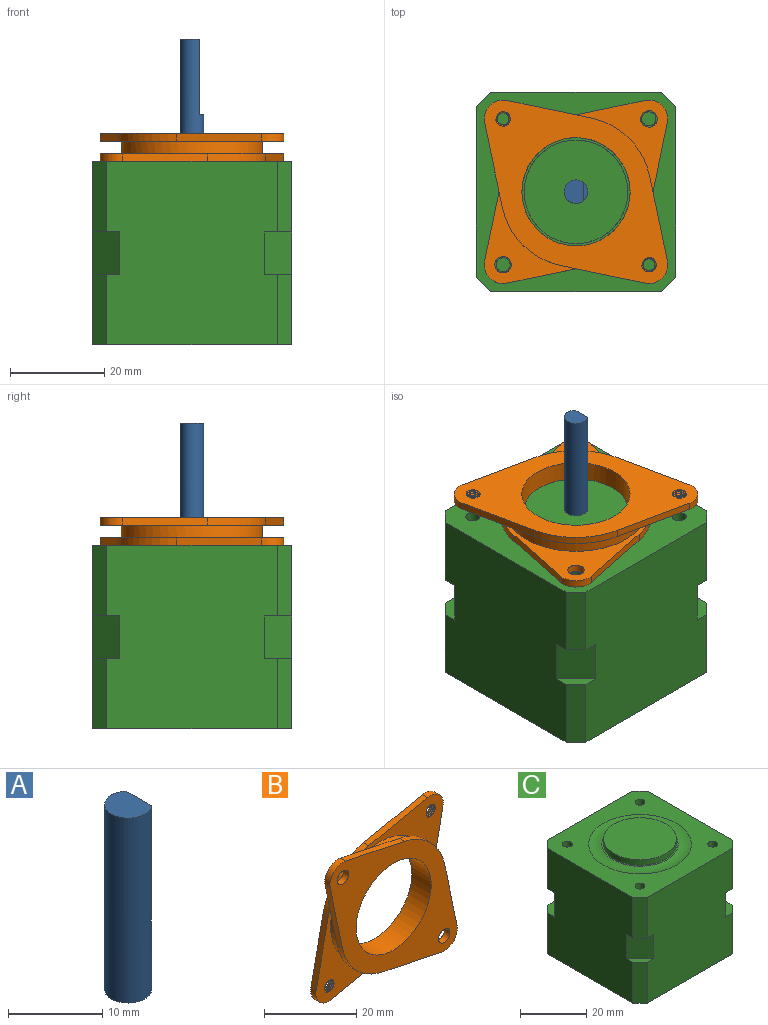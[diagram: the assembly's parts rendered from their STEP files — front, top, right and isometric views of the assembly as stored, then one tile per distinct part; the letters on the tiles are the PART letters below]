
ASSEMBLY  parts=3 mates=2
PART A: 5 faces, bbox 5x5x24 mm
  f0: cylinder r=2.5mm len=24mm, axis (0,0,-1), area 306.9mm2, adj f1,f2,f3,f4
  f1: plane 5x4.1mm, normal (0,0,1), area 17.2mm2, adj f0,f3
  f2: plane 5x5mm, normal (0,0,-1), area 19.6mm2, adj f0
  f3: plane 16x3.84mm, normal (1,0,0), area 61.5mm2, adj f0,f1,f4
  f4: plane 3.84x0.9mm, normal (0,0,1), area 2.4mm2, adj f0,f3
PART B: 32 faces, bbox 39.1x6.2x39.1 mm
  f0: cylinder r=1.75mm len=3.5mm, axis (0,1,0), area 17.6mm2, adj f10,f11
  f1: cylinder r=1.75mm len=3.5mm, axis (0,1,0), area 17.6mm2, adj f10,f11
  f2: plane 17.96x3.75mm, normal (-0.2,0,-0.98), area 29.3mm2, adj f3,f9,f10,f11
  f3: cylinder r=4mm len=4.82mm, axis (0,1,0), area 12.7mm2, adj f2,f4,f10,f11
  f4: plane 17.96x3.75mm, normal (0.98,0,0.2), area 29.3mm2, adj f3,f5,f10,f11
  f5: cylinder r=16mm len=12.39mm, axis (0,1,0), area 29.7mm2, adj f4,f6,f10,f11
  f6: plane 17.96x3.75mm, normal (0.2,0,0.98), area 29.3mm2, adj f5,f7,f10,f11
  f7: cylinder r=4mm len=4.82mm, axis (0,1,0), area 12.7mm2, adj f6,f8,f10,f11
  f8: plane 17.96x3.75mm, normal (-0.98,0,-0.2), area 29.3mm2, adj f7,f9,f10,f11
  f9: cylinder r=16mm len=12.39mm, axis (0,1,0), area 29.7mm2, adj f2,f8,f10,f11
  f10: plane 39x39mm, normal (0,1,0), area 336mm2, adj f0,f1,f2,f3,f4,f5,f6,f7
  f11: plane 39x39mm, normal (0,-1,0), area 627.4mm2, adj f0,f1,f2,f3,f4,f5,f6,f7
  f12: plane 39.14x39.14mm, normal (0,1,0), area 633.9mm2, adj f14,f15,f16,f17,f18,f19,f20,f21
  f13: cylinder r=15mm len=30mm, axis (0,1,0), area 254.5mm2, adj f10,f31
  f14: cylinder r=11.5mm len=23mm, axis (0,-1,0), area 426.3mm2, adj f11,f12
  f15: cylinder r=1.54mm len=3.09mm, axis (0,1,0), area 3.6mm2, adj f12,f16,f17,f31
  f16: bspline ~3.58x3.57mm, area 9.1mm2, adj f12,f15,f22,f31
  f17: bspline ~3.59x3.58mm, area 9.1mm2, adj f12,f15,f22,f31
  f18: cylinder r=1.54mm len=3.09mm, axis (0,1,0), area 3.6mm2, adj f12,f19,f20,f31
  f19: bspline ~3.58x3.57mm, area 9.1mm2, adj f12,f18,f21,f31
  f20: bspline ~3.59x3.58mm, area 9.1mm2, adj f12,f18,f21,f31
  f21: cylinder r=1.26mm len=2.53mm, axis (0,1,0), area 1.5mm2, adj f12,f19,f20,f31
  f22: cylinder r=1.26mm len=2.53mm, axis (0,1,0), area 1.5mm2, adj f12,f16,f17,f31
  f23: plane 17.96x3.75mm, normal (0.2,0,-0.98), area 29.3mm2, adj f12,f24,f30,f31
  f24: cylinder r=16mm len=12.39mm, axis (0,1,0), area 29.7mm2, adj f12,f23,f25,f31
  f25: plane 17.96x3.75mm, normal (0.98,0,-0.2), area 29.3mm2, adj f12,f24,f26,f31
  f26: cylinder r=4mm len=4.82mm, axis (0,1,0), area 12.7mm2, adj f12,f25,f27,f31
  f27: plane 17.96x3.75mm, normal (-0.2,0,0.98), area 29.3mm2, adj f12,f26,f28,f31
  f28: cylinder r=16mm len=12.39mm, axis (0,1,0), area 29.7mm2, adj f12,f27,f29,f31
  f29: plane 17.96x3.75mm, normal (-0.98,0,0.2), area 29.3mm2, adj f12,f28,f30,f31
  f30: cylinder r=4mm len=4.82mm, axis (0,1,0), area 12.7mm2, adj f12,f23,f29,f31
  f31: plane 39.14x39.14mm, normal (0,-1,0), area 342.6mm2, adj f13,f15,f16,f17,f18,f19,f20,f21
PART C: 58 faces, bbox 42.3x42.3x41.1 mm
  f0: cylinder r=2.5mm len=5mm, axis (0,0,1), area 15.7mm2, adj f1,f16
  f1: plane 5x5mm, normal (0,0,-1), area 19.6mm2, adj f0
  f2: plane 5.83x5.83mm, normal (0,0,1), area 12.5mm2, adj f5,f6,f7,f33
  f3: plane 5.83x5.83mm, normal (0,0,1), area 12.5mm2, adj f5,f11,f12,f34
  f4: plane 5.83x5.83mm, normal (0,0,1), area 12.5mm2, adj f9,f10,f11,f35
  f5: plane 39x36.3mm, normal (0,1,0), area 1364.8mm2, adj f2,f3,f6,f12,f14,f33,f34,f37
  f6: plane 15x3mm, normal (-0.71,0.71,0), area 63.6mm2, adj f2,f5,f7,f14
  f7: plane 39x36.3mm, normal (-1,0,0), area 1364.8mm2, adj f2,f6,f8,f13,f14,f33,f36,f37
  f8: plane 15x3mm, normal (-0.71,-0.71,0), area 63.6mm2, adj f7,f9,f13,f14
  f9: plane 39x36.3mm, normal (0,-1,0), area 1364.8mm2, adj f4,f8,f10,f13,f14,f35,f36,f37
  f10: plane 15x3mm, normal (0.71,-0.71,0), area 63.6mm2, adj f4,f9,f11,f14
  f11: plane 39x36.3mm, normal (1,0,0), area 1364.8mm2, adj f3,f4,f10,f12,f14,f34,f35,f37
  f12: plane 15x3mm, normal (0.71,0.71,0), area 63.6mm2, adj f3,f5,f11,f14
  f13: plane 5.83x5.83mm, normal (0,0,1), area 12.5mm2, adj f7,f8,f9,f36
  f14: plane 42.3x42.3mm, normal (0,0,-1), area 1626mm2, adj f5,f6,f7,f8,f9,f10,f11,f12
  f15: cylinder r=4mm len=8mm, axis (0,0,-1), area 50.3mm2, adj f14,f16
  f16: plane 8x8mm, normal (0,0,-1), area 30.6mm2, adj f0,f15
  f17: plane 5.5x5.5mm, normal (0,0,-1), area 16.7mm2, adj f18,f26
  f18: cylinder r=2.75mm len=5.5mm, axis (0,0,-1), area 17.3mm2, adj f14,f17
  f19: plane 5.5x5.5mm, normal (0,0,-1), area 16.7mm2, adj f20,f28
  f20: cylinder r=2.75mm len=5.5mm, axis (0,0,-1), area 17.3mm2, adj f14,f19
  f21: plane 5.5x5.5mm, normal (0,0,-1), area 16.7mm2, adj f22,f30
  f22: cylinder r=2.75mm len=5.5mm, axis (0,0,-1), area 17.3mm2, adj f14,f21
  f23: plane 5.5x5.5mm, normal (0,0,-1), area 16.7mm2, adj f24,f32
  f24: cylinder r=2.75mm len=5.5mm, axis (0,0,-1), area 17.3mm2, adj f14,f23
  f25: plane 3x3mm, normal (0,0,-1), area 7.1mm2, adj f26
  f26: cylinder r=1.5mm len=4.5mm, axis (0,0,-1), area 42.4mm2, adj f17,f25
  f27: plane 3x3mm, normal (0,0,-1), area 7.1mm2, adj f28
  f28: cylinder r=1.5mm len=4.5mm, axis (0,0,-1), area 42.4mm2, adj f19,f27
  f29: plane 3x3mm, normal (0,0,-1), area 7.1mm2, adj f30
  f30: cylinder r=1.5mm len=4.5mm, axis (0,0,-1), area 42.4mm2, adj f21,f29
  f31: plane 3x3mm, normal (0,0,-1), area 7.1mm2, adj f32
  f32: cylinder r=1.5mm len=4.5mm, axis (0,0,-1), area 42.4mm2, adj f23,f31
  f33: plane 9x5.83mm, normal (-0.71,0.71,0), area 74.2mm2, adj f2,f5,f7,f40
  f34: plane 9x5.83mm, normal (0.71,0.71,0), area 74.2mm2, adj f3,f5,f11,f39
  f35: plane 9x5.83mm, normal (0.71,-0.71,0), area 74.2mm2, adj f4,f9,f11,f38
  f36: plane 9x5.83mm, normal (-0.71,-0.71,0), area 74.2mm2, adj f7,f9,f13,f45
  f37: plane 42.3x42.3mm, normal (0,0,1), area 988.2mm2, adj f5,f7,f9,f11,f41,f42,f43,f44
  f38: plane 5.83x5.83mm, normal (0,0,-1), area 12.5mm2, adj f9,f11,f35,f43
  f39: plane 5.83x5.83mm, normal (0,0,-1), area 12.5mm2, adj f5,f11,f34,f42
  f40: plane 5.83x5.83mm, normal (0,0,-1), area 12.5mm2, adj f5,f7,f33,f41
  f41: plane 15x3mm, normal (-0.71,0.71,0), area 63.6mm2, adj f5,f7,f37,f40
  f42: plane 15x3mm, normal (0.71,0.71,0), area 63.6mm2, adj f5,f11,f37,f39
  f43: plane 15x3mm, normal (0.71,-0.71,0), area 63.6mm2, adj f9,f11,f37,f38
  f44: plane 15x3mm, normal (-0.71,-0.71,0), area 63.6mm2, adj f7,f9,f37,f45
  f45: plane 5.83x5.83mm, normal (0,0,-1), area 12.5mm2, adj f7,f9,f36,f44
  f46: cylinder r=1.5mm len=5.5mm, axis (0,0,1), area 51.8mm2, adj f37,f47
  f47: plane 3x3mm, normal (0,0,1), area 7.1mm2, adj f46
  f48: cylinder r=1.5mm len=5.5mm, axis (0,0,1), area 51.8mm2, adj f37,f49
  f49: plane 3x3mm, normal (0,0,1), area 7.1mm2, adj f48
  f50: cylinder r=1.5mm len=5.5mm, axis (0,0,1), area 51.8mm2, adj f37,f51
  f51: plane 3x3mm, normal (0,0,1), area 7.1mm2, adj f50
  f52: cylinder r=1.5mm len=5.5mm, axis (0,0,1), area 51.8mm2, adj f37,f53
  f53: plane 3x3mm, normal (0,0,1), area 7.1mm2, adj f52
  f54: torus R=13.5mm, axis (0,0,-1), area 342.9mm2, adj f37,f55
  f55: plane 23x23mm, normal (0,0,1), area 35.3mm2, adj f54,f56
  f56: cylinder r=11mm len=22mm, axis (0,0,-1), area 138.2mm2, adj f55,f57
  f57: plane 22x22mm, normal (0,0,1), area 380.1mm2, adj f56
PLACE A t=(28.48,-0.76,-1.48)mm
PLACE B rot(axis=(1,0,0),90deg) t=(28.48,-0.76,37.52)mm
PLACE C t=(28.48,-0.76,-1.48)mm fixed
MATE fastened B.f0 <-> C.f20  axis (0,0,-1) through (43.98,14.74,37.52)mm
MATE revolute A.f0 <-> C.f0  axis (0,0,-1) through (28.48,-0.76,39.52)mm
